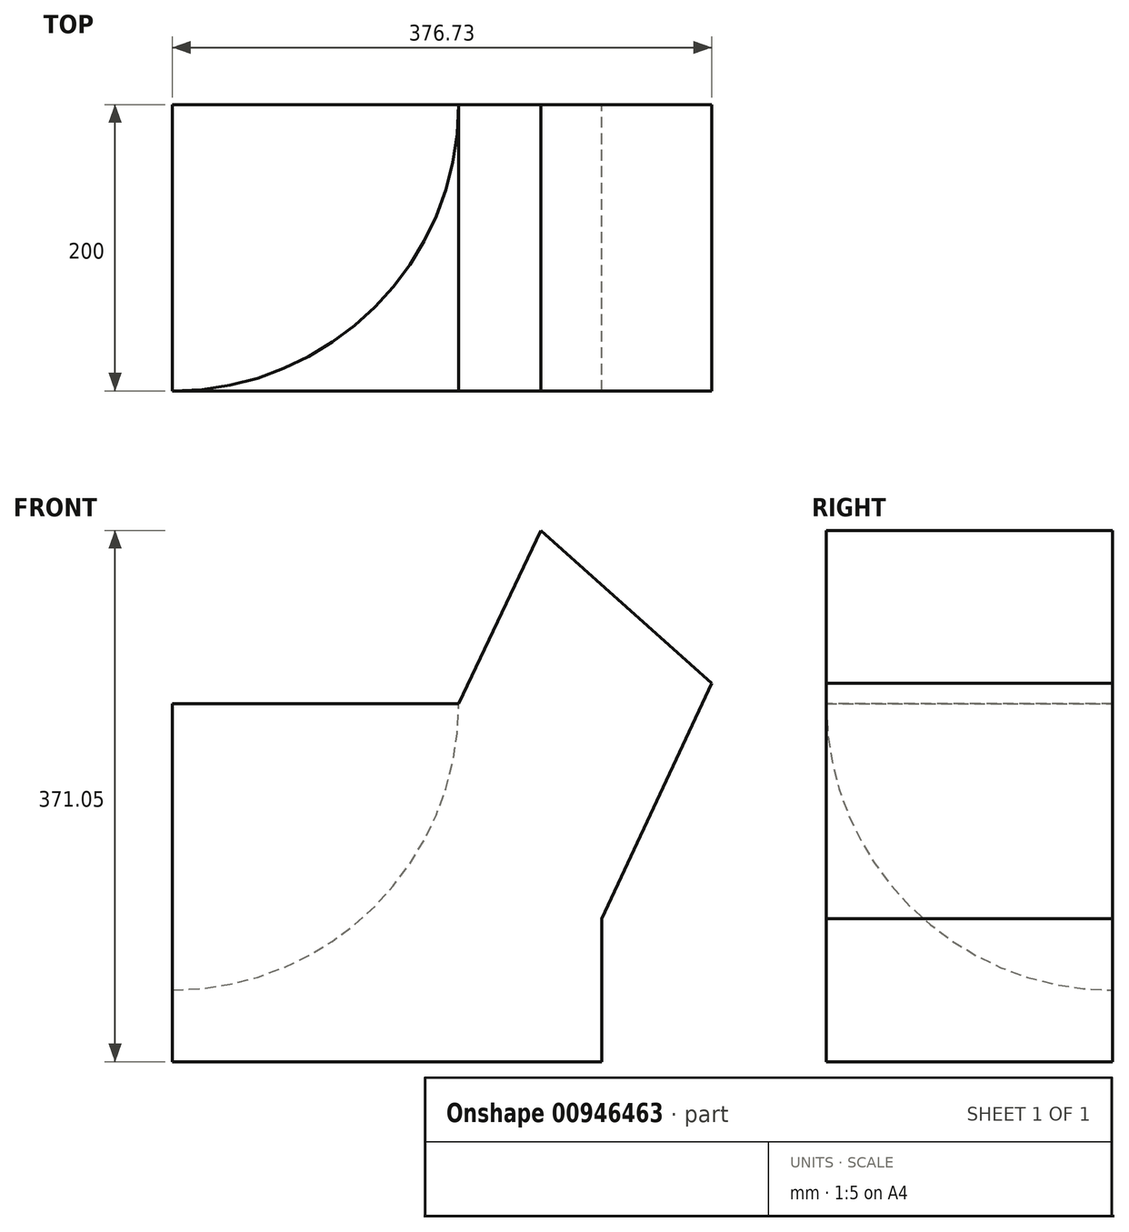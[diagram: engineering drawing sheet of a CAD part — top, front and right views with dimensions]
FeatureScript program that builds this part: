
annotation { "Feature Type Name" : "Feature", "Feature Type Description" : "" }
export const myFeature = defineFeature(function(context is Context, id is Id, definition is map)
    precondition{}
    {
        {
            var Q0;
            Q0=qCreatedBy(makeId("Front.planeOp"),FACE);
            var sketch = newSketch(context, id + "F0", { "sketchPlane" : qUnion([Q0])});
            skLineSegment(sketch, "E0.bottom", {"start": v(0, 0) * mm, "end": v(0, 0) * mm});
            skLineSegment(sketch, "E0.top", {"start": v(0, 0) * mm, "end": v(0, 0) * mm});
            skLineSegment(sketch, "E0.left", {"start": v(0, 0) * mm, "end": v(0, 0) * mm});
            skLineSegment(sketch, "E0.right", {"start": v(0, 0) * mm, "end": v(0, 0) * mm});
            skLineSegment(sketch, "E1.bottom", {"start": v(300, -250) * mm, "end": v(0, -250) * mm});
            skLineSegment(sketch, "E1.top", {"start": v(300, 0) * mm, "end": v(0, 0) * mm});
            skLineSegment(sketch, "E1.left", {"start": v(300, -250) * mm, "end": v(300, 0) * mm});
            skLineSegment(sketch, "E1.right", {"start": v(0, -250) * mm, "end": v(0, 0) * mm});
            skSolve(sketch);
        }
        {
            var Q0;
            Q0=qSketchRegion(id+"F0",true);
            extrude(context, id + "F1", {"entities" : qUnion([Q0]), "depth" : 200 * mm, "offsetDistance" : 25 * mm});
        }
        {
            var Q0;
            Q0=qCreatedBy(makeId("Front.planeOp"),FACE);
            var sketch = newSketch(context, id + "F2", { "sketchPlane" : qUnion([Q0])});
            skLineSegment(sketch, "E2", {"start": v(200, 0) * mm, "end": v(300, -150) * mm});
            skLineSegment(sketch, "E3", {"start": v(200, 0) * mm, "end": v(257.49, 121.05) * mm});
            skLineSegment(sketch, "E4", {"start": v(257.49, 121.05) * mm, "end": v(376.73, 14.41) * mm});
            skLineSegment(sketch, "E5", {"start": v(376.73, 14.41) * mm, "end": v(300, -150) * mm});
            skSolve(sketch);
        }
        {
            var Q0;
            Q0=qSketchRegion(id+"F2",true);
            extrude(context, id + "F3", {"entities" : qUnion([Q0]), "operationType" : NewBodyOperationType.ADD, "depth" : 200 * mm, "offsetDistance" : 25 * mm});
        }
        {
            var Q0;
            Q0=qCreatedBy(makeId("Top.planeOp"),FACE);
            var sketch = newSketch(context, id + "F4", { "sketchPlane" : qUnion([Q0])});
            skArc(sketch, "E6", {"start": v(0, 200) * mm, "mid": v(-200, 0) * mm, "end": v(0, -200) * mm});
            skLineSegment(sketch, "E7", {"start": v(0, 308) * mm, "end": v(0, -302.13) * mm});
            skSolve(sketch);
        }
        {
            var Q0;
            {var subQ0=sQuery(id+"F4.wireOp",EDGE,"E6");Q0=makeQuery(id+"F4.imprint","IMPRINT",FACE,{"disambiguationData":[TD([[makeQuery(id+"F4.imprint","IMPRINT",EDGE,{"derivedFrom":subQ0}),1.0]])]});}
            var Q1;
            Q1=sQuery(id+"F4.wireOp",EDGE,"E7");
            revolve(context, id + "F5", {"operationType" : NewBodyOperationType.ADD, "surfaceOperationType" : NewSurfaceOperationType.NEW, "entities" : qUnion([Q0]), "axis" : qUnion([Q1]), "revolveType" : RevolveType.FULL});
        }
    });
